# Revit family: Sanitary_Shower-Trays_Sanindusa_Stepin-Shower-Tray
name_source: partatom
category: Plumbing Fixtures
revit_build: Autodesk Revit 2018 (Build: 20170223_1515(x64)
units: mm (PartAtom-declared; Revit-internal decimal feet)

## family parameters
Always vertical = Yes
Cut with Voids When Loaded = No
OmniClass Number = 23.45.00.00
OmniClass Title = Sanitary, Laundry, and Cleaning Equipment
Part Type = Normal
Room Calculation Point = No
Round Connector Dimension = Use Diameter
Shared = No
Work Plane-Based = No

## types (1)
- Sanitary_Shower-Trays_Sanindusa_Stepin-Shower-Tray
    AssetType = Fixed
    CodePerformance = EN 14527:2006 / A1:2010
CL 2
    Color = white
    Constituents = 49911-90 shower tray drain (not included)
    Cost = 0 $
    Description = shower tray
    DrainSize = 91 mm  [stored 0.298556 ft]
    Edition number = 1
    Element Type = SHOWER: Installation or waste water appliance that emits a spray of water to wash the human body (BS6100)
    Features = "Extra flat shower tray that allows easy accessibility to the shower area. 
Glazed on all sides, except on the basis of settlement. 
Anti-slip finishing, which increases the independence, safety
and comfort in the showers area, especially for children, older people
and people with disability or reduced mobility.
Versatile application and contemporary design, also available in color black or grey."
    Finish = Non-slip
    Installation Instructions = https://www.tec.sanindusa.pt
    InstallationDate = 1900-12-31T23:59:59
    Manufacturer = Sanindusa
    ManufacturerName = Sanindusa
    ManufacturerURL = www.tec.sanindusa.pt
    Material = Fine Fireclay
    ModelNumber = 107572004AD
    ModelReference = Stepin
    Name = Stepin 120x70x3 shower tray
    NominalHeight = 32 mm  [stored 0.104987 ft]
    NominalLength = 1198 mm  [stored 3.93045 ft]
    NominalWidth = 700 mm  [stored 2.29659 ft]
    Pre-defined type (IFC) = SHOWER
    Product Guid = 556164c3-db97-4dfe-bcc9-481b15ef4f4b
    Product data url = https://bimobject.com
    ProductInformation = https://www.tec.sanindusa.pt
    ProductionYear = 2017
    Shape = rectangular
    Size = 120x70
    Type (IFC) = IfcSanitaryTerminalType
    URL = www.tec.sanindusa.pt
    Uniclass2015Code = Pr_40_20_06_84
    Uniclass2015Title = Shower trays
    Uniclass2015Version = Products v1.6
    Version = 2
    WarrantyDescription = https://www.tec.sanindusa.pt
The warranty will come into force from the moment the warranty detachable bulletin that accompanies the product is received at Sanindusa or from the moment the product is sold to the distributer
Only if the customer issues a writen and justified (Country laws, state laws, commercial strategy) request to Sanindusa, may the above mentioned warranties be the object of a possible change.
The warranty will come into force from the moment the warranty detachable bulletin that accompanies the product is received at Sanindusa or from the moment the product is sold to the distributer
Only if the customer issues a writen and justified (Country laws, state laws, commercial strategy) request to Sanindusa, may the above mentioned warranties be the object of a possible change.
    WarrantyDurationParts = 5
    WarrantyDurationUnit = year
    WarrantyStartDate = 1900-12-31T23:59:59
1900-12-31T23:59:59
    Weight = 28.80 kg

note: [stored X ft] marks values corroborated as IEEE doubles in the binary element streams (Revit-internal decimal feet)

## geometry (parser evidence)
native form markers: Sweep x7
no freeform markers — native parametric forms only
